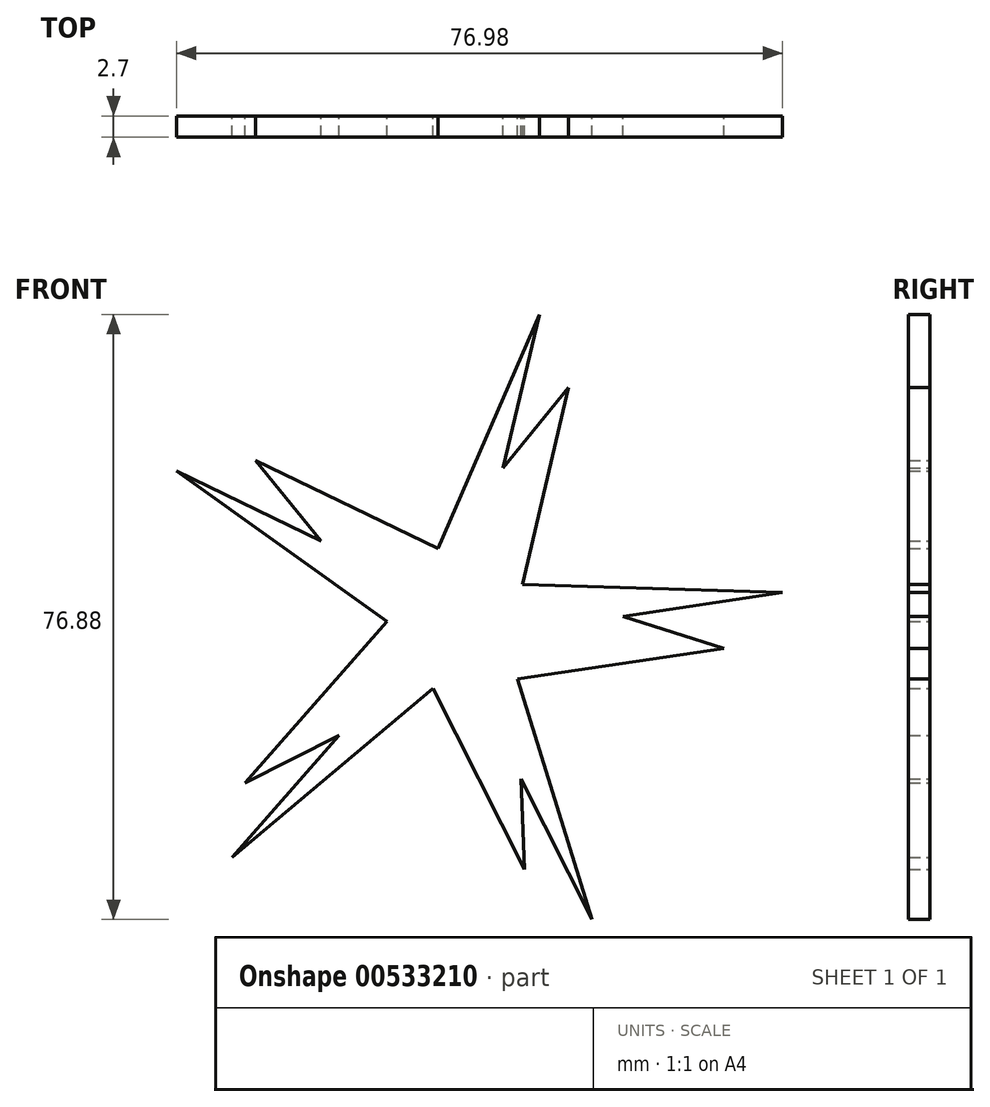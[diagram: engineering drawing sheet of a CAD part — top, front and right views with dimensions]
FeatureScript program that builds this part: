
annotation { "Feature Type Name" : "Feature", "Feature Type Description" : "" }
export const myFeature = defineFeature(function(context is Context, id is Id, definition is map)
    precondition{}
    {
        {
            var Q0;
            Q0=qCreatedBy(makeId("Front.planeOp"),FACE);
            var sketch = newSketch(context, id + "F0", { "sketchPlane" : qUnion([Q0])});
            skPoint(sketch, "E0.0.midPoint", {"position": v(-9.52, 0) * mm});
            skLineSegment(sketch, "E1", {"start": v(13.53, 29.74) * mm, "end": v(5.24, 19.5) * mm});
            skLineSegment(sketch, "E2", {"start": v(-3.05, 9.26) * mm, "end": v(-26.2, 20.48) * mm});
            skLineSegment(sketch, "E3", {"start": v(-26.2, 20.48) * mm, "end": v(-17.87, 10.24) * mm});
            skLineSegment(sketch, "E4", {"start": v(-9.52, 0) * mm, "end": v(-27.53, -20.48) * mm});
            skLineSegment(sketch, "E5", {"start": v(-27.53, -20.48) * mm, "end": v(-15.6, -14.47) * mm});
            skLineSegment(sketch, "E6", {"start": v(-3.68, -8.46) * mm, "end": v(7.92, -31.45) * mm});
            skLineSegment(sketch, "E7", {"start": v(7.92, -31.45) * mm, "end": v(7.48, -19.38) * mm});
            skLineSegment(sketch, "E8", {"start": v(7.03, -7.3) * mm, "end": v(33.26, -3.39) * mm});
            skLineSegment(sketch, "E9", {"start": v(33.26, -3.39) * mm, "end": v(20.46, 0.68) * mm});
            skLineSegment(sketch, "E10", {"start": v(13.53, 29.74) * mm, "end": v(7.66, 4.74) * mm});
            skPoint(sketch, "E11.cCircle.center.orphan", {"position": v(0, 0) * mm});
            skLineSegment(sketch, "E12", {"start": v(5.24, 19.5) * mm, "end": v(9.83, 39.03) * mm});
            skLineSegment(sketch, "E13", {"start": v(9.83, 39.03) * mm, "end": v(-3.05, 9.26) * mm});
            skLineSegment(sketch, "E14", {"start": v(-17.87, 10.24) * mm, "end": v(-36.26, 19.15) * mm});
            skLineSegment(sketch, "E15", {"start": v(-36.26, 19.15) * mm, "end": v(-9.52, 0) * mm});
            skLineSegment(sketch, "E16", {"start": v(-15.6, -14.47) * mm, "end": v(-29.23, -29.96) * mm});
            skLineSegment(sketch, "E17", {"start": v(-29.23, -29.96) * mm, "end": v(-3.68, -8.46) * mm});
            skLineSegment(sketch, "E18", {"start": v(7.48, -19.96) * mm, "end": v(16.49, -37.85) * mm});
            skPoint(sketch, "E18.startSnap0", {"position": v(7.48, -19.38) * mm});
            skPoint(sketch, "E18.startSnap1", {"position": v(2.12, -19.96) * mm});
            skLineSegment(sketch, "E19", {"start": v(16.49, -37.85) * mm, "end": v(7.03, -7.3) * mm});
            skLineSegment(sketch, "E20", {"start": v(20.46, 0.68) * mm, "end": v(40.72, 3.7) * mm});
            skLineSegment(sketch, "E21", {"start": v(40.72, 3.7) * mm, "end": v(7.66, 4.74) * mm});
            skSolve(sketch);
        }
        {
            var Q0;
            Q0=makeQuery(id+"F0.imprint","IMPRINT",FACE,{"disambiguationData":[TD([[makeQuery(id+"F0.imprint","IMPRINT",EDGE,{"derivedFrom":sQuery(id+"F0.wireOp",EDGE,"E1")}),1.0]])]});
            extrude(context, id + "F1", {"entities" : qUnion([Q0]), "depth" : 2.7 * mm, "offsetDistance" : 25 * mm});
        }
    });
